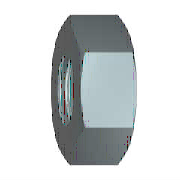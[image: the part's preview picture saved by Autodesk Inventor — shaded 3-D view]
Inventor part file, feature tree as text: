
AUTODESK INVENTOR PART (.ipt)
format: ipt  version: 2022 (Build 260153000, 153)  size: 172,544 bytes
history: native  units: mm (DEFAULTED — no unit token found)
features: sketch x3, other x2, extrude x1, hole x1, plane x1
ambient origin geometry x7: Origin, YZ Plane, XZ Plane, X Axis, Y Axis, Z Axis, Center Point
bodies: Solid1 (feature_tree)
feature tree (8):
  extrude  "Базовый элемент"  Depth=3.695042mm
  other  "Фаска1"
  hole  "Резьба"  [1 undecoded]
  other  "Work Axis1"
  plane  "Work Plane1"
  sketch  "Эскиз1"
  sketch  "Эскиз2"
  sketch  "Эскиз3"
note: 1 required parameter value undecoded (feature->parameter linkage not recoverable at this tier; creation-order binding heuristic only, values carry confidence <= 0.55)
